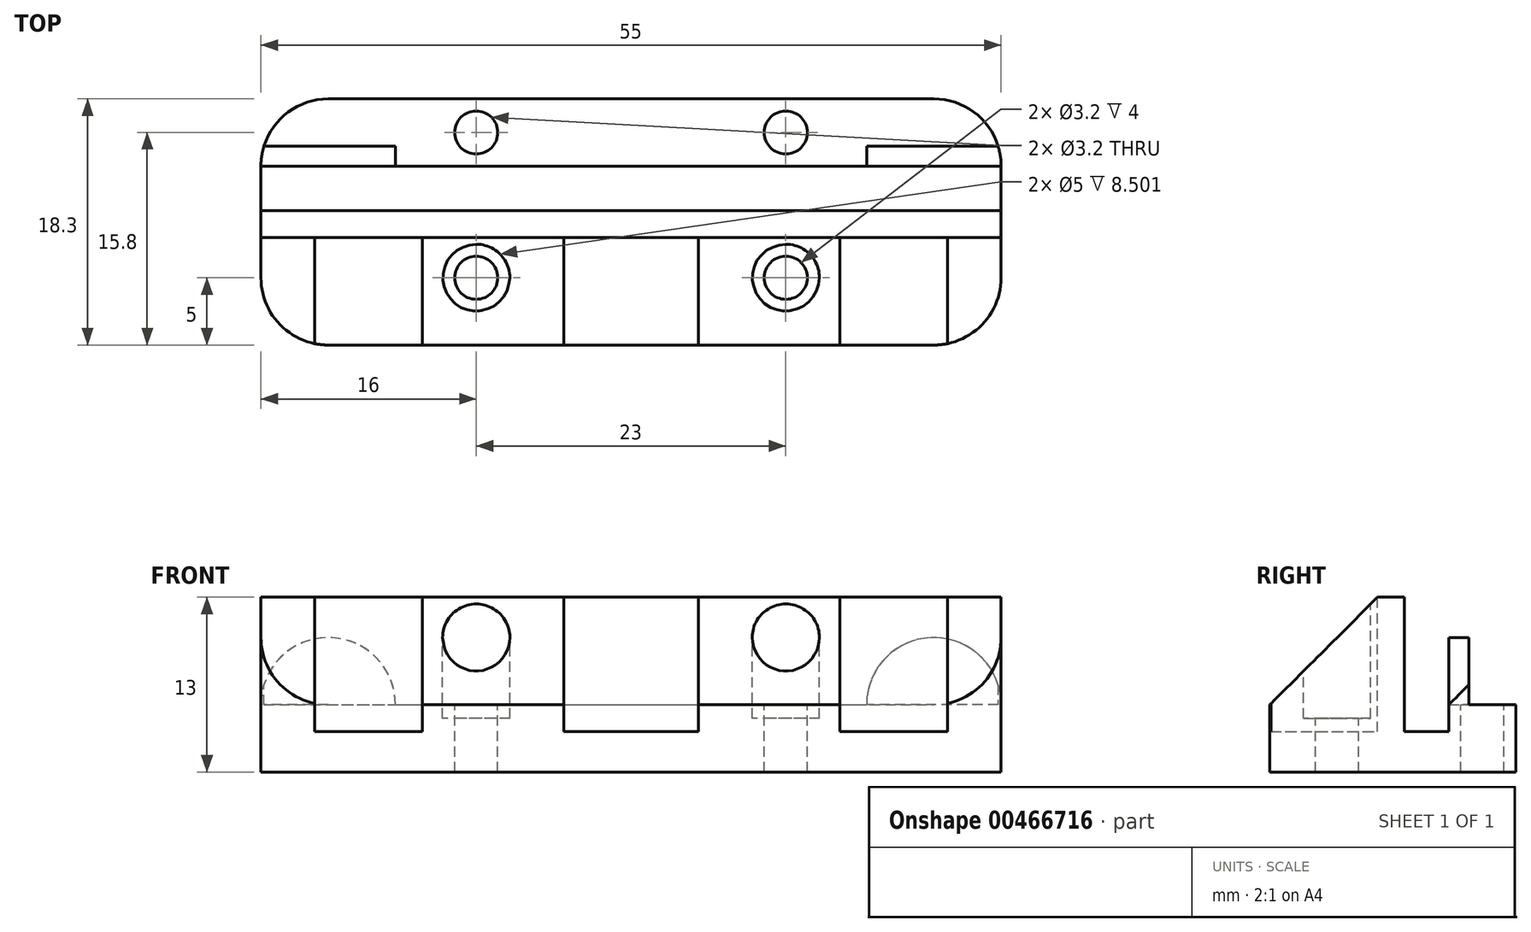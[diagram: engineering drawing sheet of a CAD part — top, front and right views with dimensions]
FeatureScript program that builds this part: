
annotation { "Feature Type Name" : "Feature", "Feature Type Description" : "" }
export const myFeature = defineFeature(function(context is Context, id is Id, definition is map)
    precondition{}
    {
        {
            var Q0;
            Q0=qCreatedBy(makeId("Top.planeOp"),FACE);
            var sketch = newSketch(context, id + "F0", { "sketchPlane" : qUnion([Q0])});
            skLineSegment(sketch, "E0.bottom", {"start": v(-27.5, 9.15) * mm, "end": v(27.5, 9.15) * mm});
            skLineSegment(sketch, "E0.top", {"start": v(-27.5, -9.15) * mm, "end": v(27.5, -9.15) * mm});
            skLineSegment(sketch, "E0.left", {"start": v(-27.5, 9.15) * mm, "end": v(-27.5, -9.15) * mm});
            skLineSegment(sketch, "E0.right", {"start": v(27.5, 9.15) * mm, "end": v(27.5, -9.15) * mm});
            skPoint(sketch, "E0.middle", {"position": v(0, 0) * mm});
            skSolve(sketch);
        }
        {
            var Q0;
            Q0 = qSketchRegion(id + "F0", true);
            extrude(context, id + "F1", {"entities" : qUnion([Q0]), "depth" : 3 * mm});
        }
        {
            var Q0;
            Q0=makeQuery(id+"F1.opExtrude","CAP_FACE",FACE,{"disambiguationData":[OSD([sQuery(id+"F0.wireOp",EDGE,"E0.bottom"),sQuery(id+"F0.wireOp",EDGE,"E0.top"),sQuery(id+"F0.wireOp",EDGE,"E0.left"),sQuery(id+"F0.wireOp",EDGE,"E0.right")])],"isStart":false});
            var sketch = newSketch(context, id + "F2", { "sketchPlane" : qUnion([Q0])});
            skLineSegment(sketch, "E1.bottom", {"start": v(-27.5, 9.15) * mm, "end": v(27.5, 9.15) * mm});
            skLineSegment(sketch, "E1.top", {"start": v(-27.5, 4.15) * mm, "end": v(27.5, 4.15) * mm});
            skLineSegment(sketch, "E1.left", {"start": v(-27.5, 9.15) * mm, "end": v(-27.5, 4.15) * mm});
            skLineSegment(sketch, "E1.right", {"start": v(27.5, 9.15) * mm, "end": v(27.5, 4.15) * mm});
            skSolve(sketch);
        }
        {
            var Q0;
            Q0 = qSketchRegion(id + "F2", true);
            extrude(context, id + "F3", {"entities" : qUnion([Q0]), "operationType" : NewBodyOperationType.ADD, "depth" : 2 * mm});
        }
        {
            var Q0;
            Q0=makeQuery(id+"F1.opExtrude","CAP_FACE",FACE,{"disambiguationData":[OSD([sQuery(id+"F0.wireOp",EDGE,"E0.bottom"),sQuery(id+"F0.wireOp",EDGE,"E0.top"),sQuery(id+"F0.wireOp",EDGE,"E0.left"),sQuery(id+"F0.wireOp",EDGE,"E0.right")])],"isStart":false});
            var sketch = newSketch(context, id + "F4", { "sketchPlane" : qUnion([Q0])});
            skLineSegment(sketch, "E2.bottom", {"start": v(-27.5, -9.15) * mm, "end": v(27.5, -9.15) * mm});
            skLineSegment(sketch, "E2.top", {"start": v(-27.5, 0.85) * mm, "end": v(27.5, 0.85) * mm});
            skLineSegment(sketch, "E2.left", {"start": v(-27.5, -9.15) * mm, "end": v(-27.5, 0.85) * mm});
            skLineSegment(sketch, "E2.right", {"start": v(27.5, -9.15) * mm, "end": v(27.5, 0.85) * mm});
            skSolve(sketch);
        }
        {
            var Q0;
            Q0 = qSketchRegion(id + "F4", true);
            extrude(context, id + "F5", {"entities" : qUnion([Q0]), "operationType" : NewBodyOperationType.ADD, "depth" : 1 * mm});
        }
        {
            var Q0;
            Q0=makeQuery(id+"F3.opExtrude","CAP_FACE",FACE,{"disambiguationData":[OSD([sQuery(id+"F2.wireOp",EDGE,"E1.bottom"),sQuery(id+"F2.wireOp",EDGE,"E1.top"),sQuery(id+"F2.wireOp",EDGE,"E1.left"),sQuery(id+"F2.wireOp",EDGE,"E1.right")])],"isStart":false});
            var sketch = newSketch(context, id + "F6", { "sketchPlane" : qUnion([Q0])});
            skLineSegment(sketch, "E3.bottom", {"start": v(27.5, 4.15) * mm, "end": v(17.5, 4.15) * mm});
            skLineSegment(sketch, "E3.top", {"start": v(27.5, 5.65) * mm, "end": v(17.5, 5.65) * mm});
            skLineSegment(sketch, "E3.left", {"start": v(27.5, 4.15) * mm, "end": v(27.5, 5.65) * mm});
            skLineSegment(sketch, "E3.right", {"start": v(17.5, 4.15) * mm, "end": v(17.5, 5.65) * mm});
            skLineSegment(sketch, "E4.bottom", {"start": v(-27.5, 4.15) * mm, "end": v(-17.5, 4.15) * mm});
            skLineSegment(sketch, "E4.top", {"start": v(-27.5, 5.65) * mm, "end": v(-17.5, 5.65) * mm});
            skLineSegment(sketch, "E4.left", {"start": v(-27.5, 4.15) * mm, "end": v(-27.5, 5.65) * mm});
            skLineSegment(sketch, "E4.right", {"start": v(-17.5, 4.15) * mm, "end": v(-17.5, 5.65) * mm});
            skSolve(sketch);
        }
        {
            var Q0;
            Q0 = qSketchRegion(id + "F6", true);
            extrude(context, id + "F7", {"entities" : qUnion([Q0]), "operationType" : NewBodyOperationType.ADD, "depth" : 5 * mm});
        }
        {
            var Q0;
            Q0=makeQuery(id+"F7.opExtrude","CAP_EDGE",EDGE,{"disambiguationData":[OSD([sQuery(id+"F6.wireOp",EDGE,"E3.right")])],"isStart":false});
            var Q1;
            Q1=makeQuery(id+"F7.opExtrude","CAP_EDGE",EDGE,{"disambiguationData":[OSD([sQuery(id+"F6.wireOp",EDGE,"E3.left")])],"isStart":false});
            var Q2;
            Q2=makeQuery(id+"F7.opExtrude","CAP_EDGE",EDGE,{"disambiguationData":[OSD([sQuery(id+"F6.wireOp",EDGE,"E4.left")])],"isStart":false});
            var Q3;
            Q3=makeQuery(id+"F7.opExtrude","CAP_EDGE",EDGE,{"disambiguationData":[OSD([sQuery(id+"F6.wireOp",EDGE,"E4.right")])],"isStart":false});
            fillet(context, id + "F8", {"entities" : qUnion([Q0, Q1, Q2, Q3]), "radius" : 5 * mm, "tangentPropagation" : true, "allowEdgeOverflow" : false});
        }
        {
            var Q0;
            Q0=makeQuery(id+"F5.opExtrude","CAP_FACE",FACE,{"disambiguationData":[OSD([sQuery(id+"F4.wireOp",EDGE,"E2.bottom"),sQuery(id+"F4.wireOp",EDGE,"E2.top"),sQuery(id+"F4.wireOp",EDGE,"E2.left"),sQuery(id+"F4.wireOp",EDGE,"E2.right")])],"isStart":false});
            extrude(context, id + "F9", {"entities" : qUnion([Q0]), "operationType" : NewBodyOperationType.ADD, "depth" : 9 * mm});
        }
        {
            var Q0;
            Q0=makeQuery(id+"F3.opExtrude","CAP_FACE",FACE,{"disambiguationData":[OSD([sQuery(id+"F2.wireOp",EDGE,"E1.bottom"),sQuery(id+"F2.wireOp",EDGE,"E1.top"),sQuery(id+"F2.wireOp",EDGE,"E1.left"),sQuery(id+"F2.wireOp",EDGE,"E1.right")])],"isStart":false});
            var sketch = newSketch(context, id + "F10", { "sketchPlane" : qUnion([Q0])});
            skSolve(sketch);
        }
        {
            var Q0;
            {var subQ3=sQuery(id+"F2.wireOp",EDGE,"E1.bottom");Q0=makeQuery(id+"F10.imprint","IMPRINT",FACE,{"disambiguationData":[TD([[makeQuery(id+"F10.imprint","IMPRINT",EDGE,{"derivedFrom":makeQuery(id+"F3.opExtrude","CAP_EDGE",EDGE,{"disambiguationData":[OSD([subQ3])],"isStart":false})}),-1.0]])]});}
            var sketch = newSketch(context, id + "F11", { "sketchPlane" : qUnion([Q0])});
            skCircle(sketch, "E5", {"center": v(11.5, 6.65) * mm, "radius": 1.6 * mm});
            skCircle(sketch, "E6", {"center": v(-11.5, 6.65) * mm, "radius": 1.6 * mm});
            skSolve(sketch);
        }
        {
            var Q0;
            Q0 = qSketchRegion(id + "F11", true);
            extrude(context, id + "F12", {"entities" : qUnion([Q0]), "operationType" : NewBodyOperationType.REMOVE, "oppositeDirection" : true, "depth" : 5 * mm});
        }
        {
            var Q0;
            Q0=makeQuery(id+"F9.opExtrude","CAP_FACE",FACE,{"disambiguationData":[OSD([sQuery(id+"F4.wireOp",EDGE,"E2.bottom"),sQuery(id+"F4.wireOp",EDGE,"E2.top"),sQuery(id+"F4.wireOp",EDGE,"E2.left"),sQuery(id+"F4.wireOp",EDGE,"E2.right")])],"isStart":false});
            var sketch = newSketch(context, id + "F13", { "sketchPlane" : qUnion([Q0])});
            skCircle(sketch, "E7", {"center": v(11.5, -4.15) * mm, "radius": 1.6 * mm});
            skCircle(sketch, "E8", {"center": v(-11.5, -4.15) * mm, "radius": 1.6 * mm});
            skSolve(sketch);
        }
        {
            var Q0;
            Q0 = qSketchRegion(id + "F13", true);
            extrude(context, id + "F14", {"entities" : qUnion([Q0]), "operationType" : NewBodyOperationType.REMOVE, "oppositeDirection" : true, "depth" : 13 * mm});
        }
        {
            var Q0;
            Q0=makeQuery(id+"F9.opExtrude","CAP_FACE",FACE,{"disambiguationData":[OSD([sQuery(id+"F4.wireOp",EDGE,"E2.bottom"),sQuery(id+"F4.wireOp",EDGE,"E2.top"),sQuery(id+"F4.wireOp",EDGE,"E2.left"),sQuery(id+"F4.wireOp",EDGE,"E2.right")])],"isStart":false});
            var sketch = newSketch(context, id + "F15", { "sketchPlane" : qUnion([Q0])});
            skLineSegment(sketch, "E9.bottom", {"start": v(5, -9.15) * mm, "end": v(-5, -9.15) * mm});
            skLineSegment(sketch, "E9.top", {"start": v(5, -1.15) * mm, "end": v(-5, -1.15) * mm});
            skLineSegment(sketch, "E9.left", {"start": v(5, -9.15) * mm, "end": v(5, -1.15) * mm});
            skLineSegment(sketch, "E9.right", {"start": v(-5, -9.15) * mm, "end": v(-5, -1.15) * mm});
            skLineSegment(sketch, "E10.bottom", {"start": v(23.5, -9.15) * mm, "end": v(15.5, -9.15) * mm});
            skLineSegment(sketch, "E10.top", {"start": v(23.5, -1.15) * mm, "end": v(15.5, -1.15) * mm});
            skLineSegment(sketch, "E10.left", {"start": v(23.5, -9.15) * mm, "end": v(23.5, -1.15) * mm});
            skLineSegment(sketch, "E10.right", {"start": v(15.5, -9.15) * mm, "end": v(15.5, -1.15) * mm});
            skLineSegment(sketch, "E11.bottom", {"start": v(-15.5, -9.15) * mm, "end": v(-23.5, -9.15) * mm});
            skLineSegment(sketch, "E11.top", {"start": v(-15.5, -1.15) * mm, "end": v(-23.5, -1.15) * mm});
            skLineSegment(sketch, "E11.left", {"start": v(-15.5, -9.15) * mm, "end": v(-15.5, -1.15) * mm});
            skLineSegment(sketch, "E11.right", {"start": v(-23.5, -9.15) * mm, "end": v(-23.5, -1.15) * mm});
            skSolve(sketch);
        }
        {
            var Q0;
            Q0 = qSketchRegion(id + "F15", true);
            extrude(context, id + "F16", {"entities" : qUnion([Q0]), "operationType" : NewBodyOperationType.REMOVE, "oppositeDirection" : true, "depth" : 10 * mm});
        }
        {
            var Q0;
            Q0=makeQuery(id+"F9.opExtrude","CAP_FACE",FACE,{"disambiguationData":[OSD([sQuery(id+"F4.wireOp",EDGE,"E2.bottom"),sQuery(id+"F4.wireOp",EDGE,"E2.top"),sQuery(id+"F4.wireOp",EDGE,"E2.left"),sQuery(id+"F4.wireOp",EDGE,"E2.right")])],"isStart":false});
            var sketch = newSketch(context, id + "F17", { "sketchPlane" : qUnion([Q0])});
            skCircle(sketch, "E12", {"center": v(11.5, -4.15) * mm, "radius": 2.5 * mm});
            skCircle(sketch, "E13", {"center": v(-11.5, -4.15) * mm, "radius": 2.5 * mm});
            skSolve(sketch);
        }
        {
            var Q0;
            Q0 = qSketchRegion(id + "F17", true);
            extrude(context, id + "F18", {"entities" : qUnion([Q0]), "operationType" : NewBodyOperationType.REMOVE, "oppositeDirection" : true, "depth" : 9 * mm});
        }
        {
            var Q0;
            {var subQ0=sQuery(id+"F4.wireOp",EDGE,"E2.bottom");Q0=makeQuery(id+"F16.boolean.opBoolean","SPLIT",EDGE,{"disambiguationData":[TD([makeQuery(id+"F1.opExtrude","SWEPT_FACE",FACE,{"disambiguationData":[OSD([sQuery(id+"F0.wireOp",EDGE,"E0.right")])]})])],"derivedFrom":makeQuery(id+"F9.opExtrude","CAP_EDGE",EDGE,{"disambiguationData":[OSD([subQ0])],"isStart":false})});}
            var Q1;
            {var subQ0=sQuery(id+"F4.wireOp",EDGE,"E2.bottom");Q1=makeQuery(id+"F16.boolean.opBoolean","SPLIT",EDGE,{"disambiguationData":[TD([makeQuery(id+"F16.opExtrude","SWEPT_FACE",FACE,{"disambiguationData":[OSD([sQuery(id+"F15.wireOp",EDGE,"E9.left")])]})])],"derivedFrom":makeQuery(id+"F9.opExtrude","CAP_EDGE",EDGE,{"disambiguationData":[OSD([subQ0])],"isStart":false})});}
            var Q2;
            {var subQ0=sQuery(id+"F4.wireOp",EDGE,"E2.bottom");Q2=makeQuery(id+"F16.boolean.opBoolean","SPLIT",EDGE,{"disambiguationData":[TD([makeQuery(id+"F16.opExtrude","SWEPT_FACE",FACE,{"disambiguationData":[OSD([sQuery(id+"F15.wireOp",EDGE,"E9.right")])]})])],"derivedFrom":makeQuery(id+"F9.opExtrude","CAP_EDGE",EDGE,{"disambiguationData":[OSD([subQ0])],"isStart":false})});}
            var Q3;
            {var subQ0=sQuery(id+"F4.wireOp",EDGE,"E2.bottom");Q3=makeQuery(id+"F16.boolean.opBoolean","SPLIT",EDGE,{"disambiguationData":[TD([makeQuery(id+"F1.opExtrude","SWEPT_FACE",FACE,{"disambiguationData":[OSD([sQuery(id+"F0.wireOp",EDGE,"E0.left")])]})])],"derivedFrom":makeQuery(id+"F9.opExtrude","CAP_EDGE",EDGE,{"disambiguationData":[OSD([subQ0])],"isStart":false})});}
            chamfer(context, id + "F19", {"entities" : qUnion([Q0, Q1, Q2, Q3]), "width" : 8 * mm, "tangentPropagation" : true});
        }
        {
            var Q0;
            {var subQ0=sQuery(id+"F4.wireOp",EDGE,"E2.right");var subQ1=sQuery(id+"F4.wireOp",EDGE,"E2.bottom");Q0=makeQuery(id+"F9.boolean.opBoolean","MERGE",EDGE,{"derivedFrom":[makeQuery(id+"F5.boolean.opBoolean","MERGE",EDGE,{"derivedFrom":[makeQuery(id+"F1.opExtrude","SWEPT_EDGE",EDGE,{"disambiguationData":[OSD([sQuery(id+"F0.wireOp",EDGE,"E0.top"),sQuery(id+"F0.wireOp",EDGE,"E0.right")])]}),makeQuery(id+"F5.opExtrude","SWEPT_EDGE",EDGE,{"disambiguationData":[OSD([subQ1,subQ0])]})]}),makeQuery(id+"F9.opExtrude","SWEPT_EDGE",EDGE,{"disambiguationData":[OSD([subQ1,subQ0])]})]});}
            var Q1;
            Q1=makeQuery(id+"F3.boolean.opBoolean","MERGE",EDGE,{"derivedFrom":[makeQuery(id+"F1.opExtrude","SWEPT_EDGE",EDGE,{"disambiguationData":[OSD([sQuery(id+"F0.wireOp",EDGE,"E0.bottom"),sQuery(id+"F0.wireOp",EDGE,"E0.right")])]}),makeQuery(id+"F3.opExtrude","SWEPT_EDGE",EDGE,{"disambiguationData":[OSD([sQuery(id+"F2.wireOp",EDGE,"E1.bottom"),sQuery(id+"F2.wireOp",EDGE,"E1.right")])]})]});
            var Q2;
            Q2=makeQuery(id+"F3.boolean.opBoolean","MERGE",EDGE,{"derivedFrom":[makeQuery(id+"F1.opExtrude","SWEPT_EDGE",EDGE,{"disambiguationData":[OSD([sQuery(id+"F0.wireOp",EDGE,"E0.bottom"),sQuery(id+"F0.wireOp",EDGE,"E0.left")])]}),makeQuery(id+"F3.opExtrude","SWEPT_EDGE",EDGE,{"disambiguationData":[OSD([sQuery(id+"F2.wireOp",EDGE,"E1.bottom"),sQuery(id+"F2.wireOp",EDGE,"E1.left")])]})]});
            var Q3;
            {var subQ0=sQuery(id+"F4.wireOp",EDGE,"E2.left");var subQ1=sQuery(id+"F4.wireOp",EDGE,"E2.bottom");Q3=makeQuery(id+"F9.boolean.opBoolean","MERGE",EDGE,{"derivedFrom":[makeQuery(id+"F5.boolean.opBoolean","MERGE",EDGE,{"derivedFrom":[makeQuery(id+"F1.opExtrude","SWEPT_EDGE",EDGE,{"disambiguationData":[OSD([sQuery(id+"F0.wireOp",EDGE,"E0.top"),sQuery(id+"F0.wireOp",EDGE,"E0.left")])]}),makeQuery(id+"F5.opExtrude","SWEPT_EDGE",EDGE,{"disambiguationData":[OSD([subQ1,subQ0])]})]}),makeQuery(id+"F9.opExtrude","SWEPT_EDGE",EDGE,{"disambiguationData":[OSD([subQ1,subQ0])]})]});}
            fillet(context, id + "F20", {"entities" : qUnion([Q0, Q1, Q2, Q3]), "radius" : 5 * mm, "tangentPropagation" : true, "allowEdgeOverflow" : false});
        }
    });
